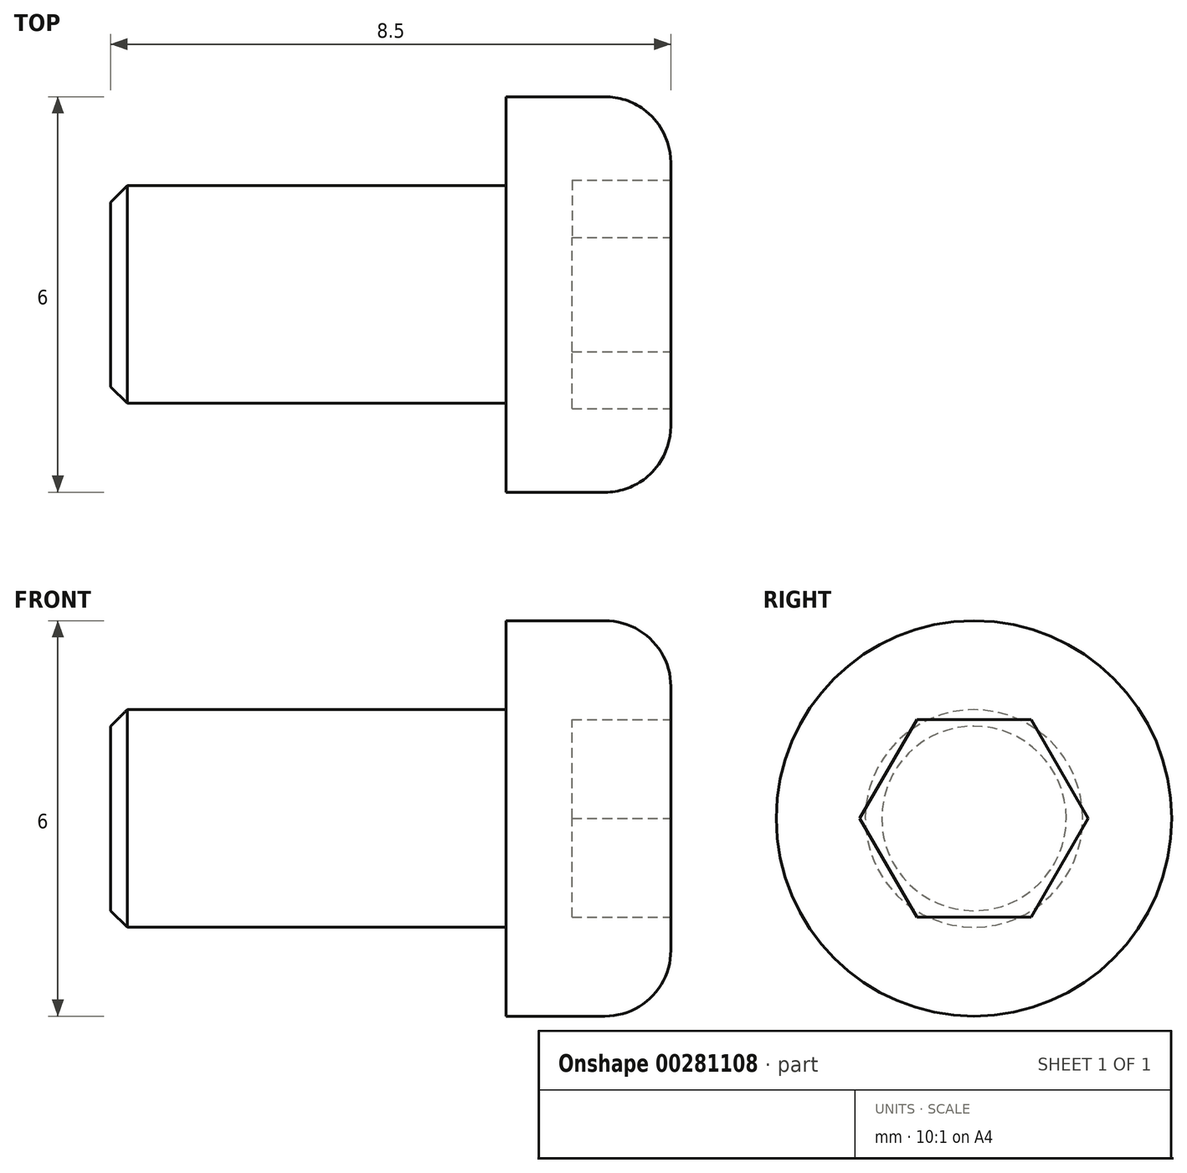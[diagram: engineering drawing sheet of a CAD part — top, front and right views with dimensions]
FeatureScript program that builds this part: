
annotation { "Feature Type Name" : "Feature", "Feature Type Description" : "" }
export const myFeature = defineFeature(function(context is Context, id is Id, definition is map)
    precondition{}
    {
        {
            var Q0;
            Q0=qCreatedBy(makeId("Front.planeOp"),FACE);
            var sketch = newSketch(context, id + "F0", { "sketchPlane" : qUnion([Q0])});
            skLineSegment(sketch, "E0", {"start": v(-4.25, 0) * mm, "end": v(-4.25, -1.65) * mm});
            skLineSegment(sketch, "E1", {"start": v(-4.25, -1.65) * mm, "end": v(1.75, -1.65) * mm});
            skLineSegment(sketch, "E2", {"start": v(1.75, -1.65) * mm, "end": v(1.75, -3) * mm});
            skLineSegment(sketch, "E3", {"start": v(1.75, -3) * mm, "end": v(4.25, -3) * mm});
            skLineSegment(sketch, "E4", {"start": v(4.25, -3) * mm, "end": v(4.25, 0) * mm});
            skLineSegment(sketch, "E5", {"start": v(4.25, 0) * mm, "end": v(-4.25, 0) * mm});
            skLineSegment(sketch, "E6", {"start": v(0, 0) * mm, "end": v(8.32, 0) * mm, "construction": true});
            skSolve(sketch);
        }
        {
            var Q0;
            Q0=makeQuery(id+"F0.imprint","IMPRINT",FACE,{"disambiguationData":[TD([[makeQuery(id+"F0.imprint","IMPRINT",EDGE,{"derivedFrom":sQuery(id+"F0.wireOp",EDGE,"E0")}),1.0]])]});
            var Q1;
            Q1=sQuery(id+"F0.wireOp",EDGE,"E6");
            revolve(context, id + "F1", {"entities" : qUnion([Q0]), "axis" : qUnion([Q1]), "revolveType" : RevolveType.FULL});
        }
        {
            var Q0;
            Q0=makeQuery(id+"F1.opRevolve","SWEPT_EDGE",EDGE,{"disambiguationData":[OSD([sQuery(id+"F0.wireOp",EDGE,"E0"),sQuery(id+"F0.wireOp",EDGE,"E1")])]});
            chamfer(context, id + "F2", {"entities" : qUnion([Q0]), "chamferType" : ChamferType.OFFSET_ANGLE, "width" : .25 * mm, "oppositeDirection" : false, "angle" : 45 * degree, "tangentPropagation" : true});
        }
        {
            var Q0;
            Q0=makeQuery(id+"F1.opRevolve","SWEPT_EDGE",EDGE,{"disambiguationData":[OSD([sQuery(id+"F0.wireOp",EDGE,"E3"),sQuery(id+"F0.wireOp",EDGE,"E4")])]});
            fillet(context, id + "F3", {"entities" : qUnion([Q0]), "radius" : 1 * mm, "tangentPropagation" : true, "allowEdgeOverflow" : false});
        }
        {
            var Q0;
            Q0=makeQuery(id+"F1.opRevolve","SWEPT_FACE",FACE,{"disambiguationData":[OSD([sQuery(id+"F0.wireOp",EDGE,"E4")])]});
            var sketch = newSketch(context, id + "F4", { "sketchPlane" : qUnion([Q0])});
            skPoint(sketch, "E7.0", {"position": v(0, 0) * mm});
            skCircle(sketch, "E8.cCircle", {"center": v(0, 0) * mm, "radius": 1.5 * mm, "construction": true});
            skLineSegment(sketch, "E8.0", {"start": v(-0.87, 1.5) * mm, "end": v(0.87, 1.5) * mm});
            skLineSegment(sketch, "E8.1", {"start": v(0.87, 1.5) * mm, "end": v(1.73, 0) * mm});
            skLineSegment(sketch, "E8.2", {"start": v(1.73, 0) * mm, "end": v(0.87, -1.5) * mm});
            skLineSegment(sketch, "E8.3", {"start": v(0.87, -1.5) * mm, "end": v(-0.87, -1.5) * mm});
            skLineSegment(sketch, "E8.4", {"start": v(-0.87, -1.5) * mm, "end": v(-1.73, 0) * mm});
            skLineSegment(sketch, "E8.5", {"start": v(-1.73, 0) * mm, "end": v(-0.87, 1.5) * mm});
            skPoint(sketch, "E8.0.midPoint", {"position": v(0, 1.5) * mm});
            skSolve(sketch);
        }
        {
            var Q0;
            Q0 = qSketchRegion(id + "F4", true);
            extrude(context, id + "F5", {"entities" : qUnion([Q0]), "operationType" : NewBodyOperationType.REMOVE, "oppositeDirection" : true, "depth" : 1.5 * mm});
        }
    });
